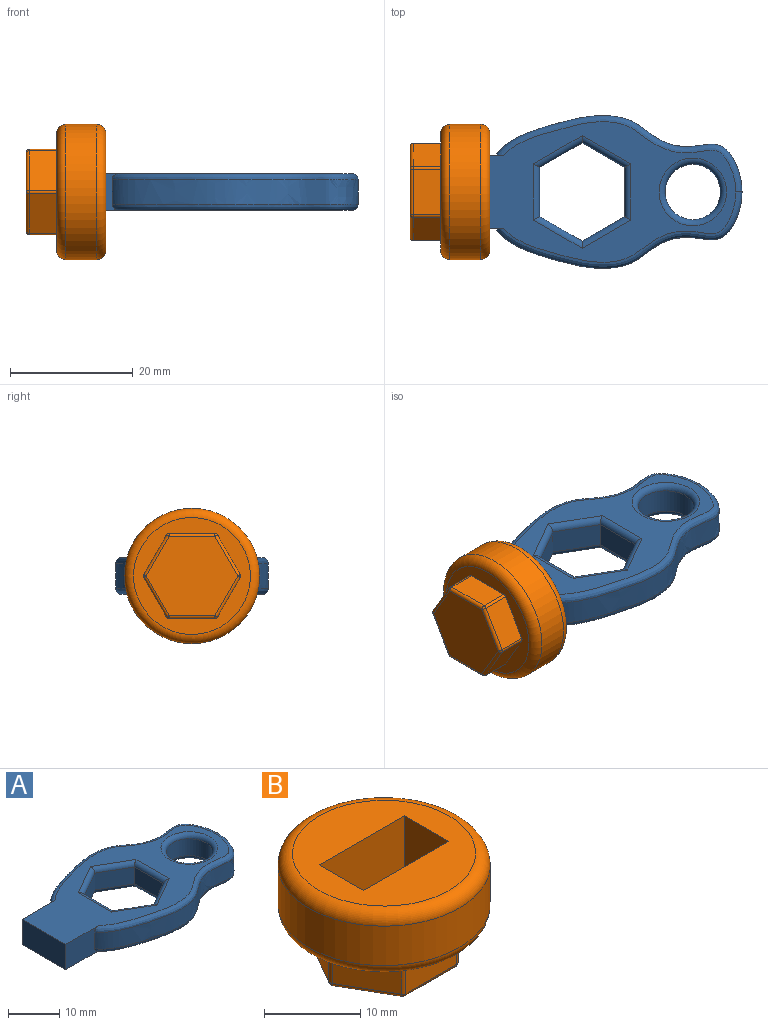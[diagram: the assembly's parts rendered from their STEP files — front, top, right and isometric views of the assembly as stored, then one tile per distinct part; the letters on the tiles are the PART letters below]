
ASSEMBLY  parts=2 mates=1
PART A: 32 faces, bbox 48.4x25.2x6.4 mm
  f0: plane 12x6mm, normal (-1,0,0), area 72mm2, adj f1,f11,f12,f13
  f1: plane 9.62x6.37mm, normal (0,-1,0), area 48.5mm2, adj f0,f2,f12,f13,f15,f24
  f2: extruded ~40x12.43mm, area 192.2mm2, adj f1,f3,f15,f24
  f3: extruded ~40x12.43mm, area 192.2mm2, adj f2,f11,f16,f25
  f4: plane 6.93x4mm, normal (-0.5,-0.87,0), area 32mm2, adj f5,f9,f20,f29
  f5: plane 8x4mm, normal (-1,0,0), area 32mm2, adj f4,f6,f18,f27
  f6: plane 6.93x4mm, normal (-0.5,0.87,0), area 32mm2, adj f5,f7,f17,f26
  f7: plane 6.93x4mm, normal (0.5,0.87,0), area 32mm2, adj f6,f8,f19,f28
  f8: plane 8x4mm, normal (1,0,0), area 32mm2, adj f7,f9,f21,f30
  f9: plane 6.93x4mm, normal (0.5,-0.87,0), area 32mm2, adj f4,f8,f22,f31
  f10: cylinder r=4.5mm len=9mm, axis (0,0,-1), area 113.1mm2, adj f14,f23
  f11: plane 9.62x6.37mm, normal (0,1,0), area 48.5mm2, adj f0,f3,f12,f13,f16,f25
  f12: plane 47x22.86mm, normal (0,0,1), area 446.9mm2, adj f0,f1,f11,f23,f24,f25,f26,f27
  f13: plane 47x22.86mm, normal (0,0,-1), area 446.9mm2, adj f0,f1,f11,f14,f15,f16,f17,f18
  f14: torus R=5.5mm, axis (0,0,1), area 48mm2, adj f10,f13
  f15: bspline ~40.69x12.66mm, area 73.4mm2, adj f1,f2,f13,f16
  f16: bspline ~40.69x12.66mm, area 73.4mm2, adj f3,f11,f13,f15
  f17: cylinder r=1mm len=8.43mm, axis (-0.87,-0.5,0), area 13.5mm2, adj f6,f13,f18,f19
  f18: cylinder r=1mm len=9.15mm, axis (0,-1,0), area 13.5mm2, adj f5,f13,f17,f20
  f19: cylinder r=1mm len=8.43mm, axis (-0.87,0.5,0), area 13.5mm2, adj f7,f13,f17,f21
  f20: cylinder r=1mm len=8.43mm, axis (0.87,-0.5,0), area 13.5mm2, adj f4,f13,f18,f22
  f21: cylinder r=1mm len=9.15mm, axis (0,1,0), area 13.5mm2, adj f8,f13,f19,f22
  f22: cylinder r=1mm len=8.43mm, axis (0.87,0.5,0), area 13.5mm2, adj f9,f13,f20,f21
  f23: torus R=5.5mm, axis (0,0,1), area 48mm2, adj f10,f12
  f24: bspline ~40.69x12.66mm, area 73.4mm2, adj f1,f2,f12,f25
  f25: bspline ~40.69x12.66mm, area 73.4mm2, adj f3,f11,f12,f24
  f26: cylinder r=1mm len=8.43mm, axis (0.87,0.5,0), area 13.5mm2, adj f6,f12,f27,f28
  f27: cylinder r=1mm len=9.15mm, axis (0,1,0), area 13.5mm2, adj f5,f12,f26,f29
  f28: cylinder r=1mm len=8.43mm, axis (0.87,-0.5,0), area 13.5mm2, adj f7,f12,f26,f30
  f29: cylinder r=1mm len=8.43mm, axis (-0.87,0.5,0), area 13.5mm2, adj f4,f12,f27,f31
  f30: cylinder r=1mm len=9.15mm, axis (0,-1,0), area 13.5mm2, adj f8,f12,f28,f31
  f31: cylinder r=1mm len=8.43mm, axis (-0.87,-0.5,0), area 13.5mm2, adj f9,f12,f29,f30
PART B: 35 faces, bbox 23.8x23.8x13 mm
  f0: plane 6.43x4.5mm, normal (0.87,0.5,0), area 33.4mm2, adj f9,f28,f32,f34
  f1: plane 7.42x4.5mm, normal (0,1,0), area 33.4mm2, adj f9,f25,f31,f34
  f2: plane 6.43x4.5mm, normal (-0.87,0.5,0), area 33.4mm2, adj f9,f19,f25,f26
  f3: plane 6.43x4.5mm, normal (-0.87,-0.5,0), area 33.4mm2, adj f9,f17,f19,f20
  f4: plane 7.42x4.5mm, normal (0,-1,0), area 33.4mm2, adj f9,f17,f21,f22
  f5: plane 6.43x4.5mm, normal (0.87,-0.5,0), area 33.4mm2, adj f9,f22,f27,f28
  f6: plane 14.85x12.86mm, normal (0,0,-1), area 143.1mm2, adj f20,f21,f26,f27,f31,f32
  f7: plane 19x19mm, normal (0,0,1), area 202.3mm2, adj f10,f11,f12,f13,f16
  f8: cylinder r=11mm len=22mm, axis (0,0,-1), area 345.6mm2, adj f15,f16
  f9: plane 19x19mm, normal (0,0,-1), area 117.3mm2, adj f0,f1,f2,f3,f4,f5,f15,f17
  f10: plane 7x6.5mm, normal (-1,0,0), area 45.5mm2, adj f7,f11,f13,f14
  f11: plane 12.5x7mm, normal (0,-1,0), area 87.5mm2, adj f7,f10,f12,f14
  f12: plane 7x6.5mm, normal (1,0,0), area 45.5mm2, adj f7,f11,f13,f14
  f13: plane 12.5x7mm, normal (0,1,0), area 87.5mm2, adj f7,f10,f12,f14
  f14: plane 12.5x6.5mm, normal (0,0,1), area 81.2mm2, adj f10,f11,f12,f13
  f15: torus R=9.5mm, axis (0,0,1), area 154.8mm2, adj f8,f9
  f16: torus R=9.5mm, axis (0,0,1), area 154.8mm2, adj f7,f8
  f17: cylinder r=0.5mm len=4.5mm, axis (0,0,1), area 2.4mm2, adj f3,f4,f9,f18
  f18: sphere r=0.5mm, area 0.3mm2, adj f17,f20,f21
  f19: cylinder r=0.5mm len=4.5mm, axis (0,0,1), area 2.4mm2, adj f2,f3,f9,f23
  f20: cylinder r=0.5mm len=6.68mm, axis (-0.5,0.87,0), area 5.8mm2, adj f3,f6,f18,f23
  f21: cylinder r=0.5mm len=7.42mm, axis (-1,0,0), area 5.8mm2, adj f4,f6,f18,f24
  f22: cylinder r=0.5mm len=4.5mm, axis (0,0,1), area 2.4mm2, adj f4,f5,f9,f24
  f23: sphere r=0.5mm, area 0.3mm2, adj f19,f20,f26
  f24: sphere r=0.5mm, area 0.3mm2, adj f21,f22,f27
  f25: cylinder r=0.5mm len=4.5mm, axis (0,0,1), area 2.4mm2, adj f1,f2,f9,f29
  f26: cylinder r=0.5mm len=6.68mm, axis (0.5,0.87,0), area 5.8mm2, adj f2,f6,f23,f29
  f27: cylinder r=0.5mm len=6.68mm, axis (-0.5,-0.87,0), area 5.8mm2, adj f5,f6,f24,f30
  f28: cylinder r=0.5mm len=4.5mm, axis (0,0,1), area 2.4mm2, adj f0,f5,f9,f30
  f29: sphere r=0.5mm, area 0.3mm2, adj f25,f26,f31
  f30: sphere r=0.5mm, area 0.3mm2, adj f27,f28,f32
  f31: cylinder r=0.5mm len=7.42mm, axis (1,0,0), area 5.8mm2, adj f1,f6,f29,f33
  f32: cylinder r=0.5mm len=6.68mm, axis (0.5,-0.87,0), area 5.8mm2, adj f0,f6,f30,f33
  f33: sphere r=0.5mm, area 0.3mm2, adj f31,f32,f34
  f34: cylinder r=0.5mm len=4.5mm, axis (0,0,1), area 2.4mm2, adj f0,f1,f9,f33
PLACE A t=(-16.94,1.83,-7.38)mm fixed
PLACE B rot(axis=(0.58,0.58,0.58),120deg) t=(-17.94,1.83,-4.38)mm
MATE fastened A.f0 <-> B.f8  axis (-1,0,0) through (-16.94,1.83,-4.38)mm
